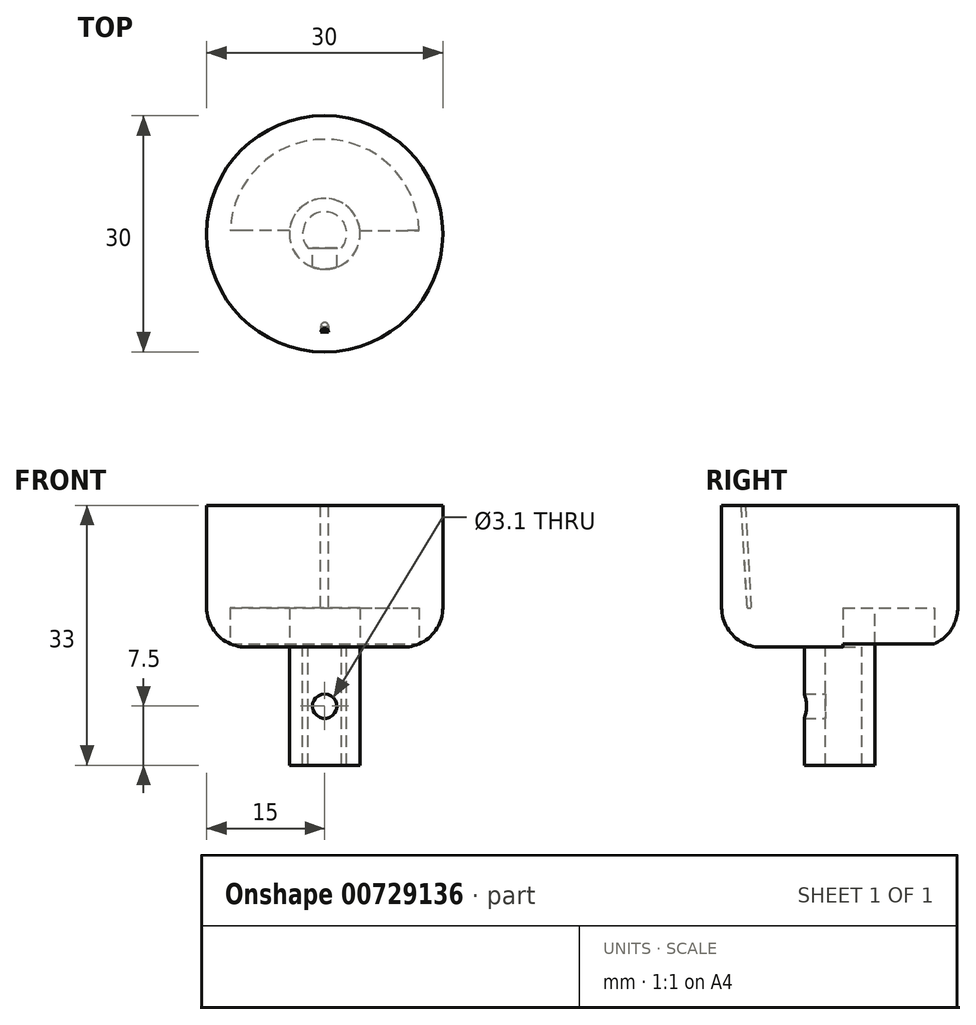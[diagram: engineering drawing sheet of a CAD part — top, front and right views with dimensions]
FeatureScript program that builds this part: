
annotation { "Feature Type Name" : "Feature", "Feature Type Description" : "" }
export const myFeature = defineFeature(function(context is Context, id is Id, definition is map)
    precondition{}
    {
        {
            var Q0;
            Q0=qCreatedBy(makeId("Top.planeOp"),FACE);
            var sketch = newSketch(context, id + "F0", { "sketchPlane" : qUnion([Q0])});
            skLineSegment(sketch, "E0", {"start": v(-2.14, -1.8) * mm, "end": v(2.14, -1.8) * mm});
            skArc(sketch, "E1", {"start": v(-2.14, -1.8) * mm, "mid": v(0, 2.8) * mm, "end": v(2.14, -1.8) * mm});
            skCircle(sketch, "E2", {"center": v(0, 0) * mm, "radius": 15 * mm});
            skCircle(sketch, "E3", {"center": v(0, 0) * mm, "radius": 4.5 * mm});
            skCircle(sketch, "E4", {"center": v(0, 0) * mm, "radius": 12 * mm});
            skSolve(sketch);
        }
        {
            var Q0;
            Q0=makeQuery(id+"F0.imprint","IMPRINT",FACE,{"disambiguationData":[TD([[makeQuery(id+"F0.imprint","IMPRINT",EDGE,{"derivedFrom":sQuery(id+"F0.wireOp",EDGE,"E0")}),-1.0]])]});
            var Q1;
            Q1=sQuery(id+"F0.wireOp",EDGE,"E1");
            var Q2;
            Q2=sQuery(id+"F0.wireOp",EDGE,"E0");
            extrude(context, id + "F1", {"entities" : qUnion([Q0]), "surfaceEntities" : qUnion([Q1, Q2]), "oppositeDirection" : true, "depth" : 15 * mm, "offsetDistance" : 25 * mm});
        }
        {
            var Q0;
            Q0=makeQuery(id+"F0.imprint","IMPRINT",FACE,{"disambiguationData":[TD([[makeQuery(id+"F0.imprint","IMPRINT",EDGE,{"derivedFrom":sQuery(id+"F0.wireOp",EDGE,"E3")}),-1.0]])]});
            var Q1;
            Q1=makeQuery(id+"F0.imprint","IMPRINT",FACE,{"disambiguationData":[TD([[makeQuery(id+"F0.imprint","IMPRINT",EDGE,{"derivedFrom":sQuery(id+"F0.wireOp",EDGE,"E0")}),1.0]])]});
            var Q2;
            Q2=makeQuery(id+"F0.imprint","IMPRINT",FACE,{"disambiguationData":[TD([[makeQuery(id+"F0.imprint","IMPRINT",EDGE,{"derivedFrom":sQuery(id+"F0.wireOp",EDGE,"E0")}),-1.0]])]});
            extrude(context, id + "F2", {"entities" : qUnion([Q0, Q1, Q2]), "operationType" : NewBodyOperationType.ADD, "depth" : 5 * mm, "offsetDistance" : 25 * mm});
        }
        {
            var Q0;
            {var subQ0=sQuery(id+"F0.wireOp",EDGE,"E0");Q0=makeQuery(id+"F2.boolean.opBoolean","MERGE",FACE,{"derivedFrom":[makeQuery(id+"F1.opExtrude","SWEPT_FACE",FACE,{"disambiguationData":[OSD([subQ0])]}),makeQuery(id+"F2.opExtrude","SWEPT_FACE",FACE,{"disambiguationData":[OSD([subQ0])]})]});}
            var sketch = newSketch(context, id + "F3", { "sketchPlane" : qUnion([Q0])});
            skPoint(sketch, "E5", {"position": v(0, -7.5) * mm});
            skSolve(sketch);
        }
        {
            var Q0;
            Q0=sQuery(id+"F3.wireOp",VERTEX,"E5");
            var Q1;
            Q1=makeQuery(id+"F1.opExtrude","SWEPT_BODY",BODY,{"disambiguationData":[OSD([sQuery(id+"F0.wireOp",EDGE,"E0"),sQuery(id+"F0.wireOp",EDGE,"E1"),sQuery(id+"F0.wireOp",EDGE,"E3")])]});
            hole(context, id + "F4", {"style" : HoleStyle.SIMPLE, "endStyle" : HoleEndStyle.THROUGH, "holeDiameter" : 3.1 * mm, "majorDiameter" : 5 * mm, "isTappedThrough" : true, "tappedDepth" : 12 * mm, "tapClearance" : 3, "locations" : qUnion([Q0]), "scope" : qUnion([Q1])});
        }
        {
            var Q0;
            Q0=qCreatedBy(makeId("Right.planeOp"),FACE);
            var sketch = newSketch(context, id + "F5", { "sketchPlane" : qUnion([Q0])});
            skLineSegment(sketch, "E6", {"start": v(11.75, 0) * mm, "end": v(15, 0) * mm});
            skLineSegment(sketch, "E7", {"start": v(15, 18) * mm, "end": v(12.5, 18) * mm});
            skLineSegment(sketch, "E8", {"start": v(15, 18) * mm, "end": v(15, 0) * mm});
            skLineSegment(sketch, "E9", {"start": v(11.75, 0) * mm, "end": v(11.75, 5) * mm});
            skLineSegment(sketch, "E10", {"start": v(11.75, 5) * mm, "end": v(12.5, 18) * mm});
            skLineSegment(sketch, "E11", {"start": v(0, 9.96) * mm, "end": v(0, -1.49) * mm, "construction": true});
            skSolve(sketch);
        }
        {
            var Q0;
            Q0=makeQuery(id+"F5.imprint","IMPRINT",FACE,{"disambiguationData":[TD([[makeQuery(id+"F5.imprint","IMPRINT",EDGE,{"derivedFrom":sQuery(id+"F5.wireOp",EDGE,"E6")}),1.0]])]});
            var Q1;
            Q1=sQuery(id+"F5.wireOp",EDGE,"E11");
            revolve(context, id + "F6", {"operationType" : NewBodyOperationType.ADD, "surfaceOperationType" : NewSurfaceOperationType.NEW, "entities" : qUnion([Q0]), "axis" : qUnion([Q1]), "revolveType" : RevolveType.FULL});
        }
        {
            var Q0;
            Q0=makeQuery(id+"F2.opExtrude","CAP_FACE",FACE,{"disambiguationData":[OSD([sQuery(id+"F0.wireOp",EDGE,"E4")])],"isStart":false});
            var sketch = newSketch(context, id + "F7", { "sketchPlane" : qUnion([Q0])});
            skCircle(sketch, "E12", {"center": v(0, 0) * mm, "radius": 11.75 * mm, "construction": true});
            skLineSegment(sketch, "E13", {"start": v(0.5, 11.74) * mm, "end": v(0.5, 11.74) * mm});
            skArc(sketch, "E14", {"start": v(-0.5, -11.74) * mm, "mid": v(0, -11.25) * mm, "end": v(0.5, -11.74) * mm});
            skSolve(sketch);
        }
        {
            var Q0;
            {var subQ0=sQuery(id+"F0.wireOp",EDGE,"E4");Q0=makeQuery(id+"F6.boolean.opBoolean","MERGE",FACE,{"derivedFrom":[makeQuery(id+"F2.boolean.opBoolean","SPLIT",FACE,{"disambiguationData":[TD([makeQuery(id+"F1.opExtrude","SWEPT_FACE",FACE,{"disambiguationData":[OSD([sQuery(id+"F0.wireOp",EDGE,"E3")])]})])],"derivedFrom":makeQuery(id+"F2.opExtrude","CAP_FACE",FACE,{"disambiguationData":[OSD([subQ0])],"isStart":true})}),makeQuery(id+"F6.opRevolve","SWEPT_FACE",FACE,{"disambiguationData":[OSD([sQuery(id+"F5.wireOp",EDGE,"E6")])]})]});}
            var sketch = newSketch(context, id + "F8", { "sketchPlane" : qUnion([Q0])});
            skCircle(sketch, "E15", {"center": v(0, 0) * mm, "radius": 12 * mm});
            skLineSegment(sketch, "E16", {"start": v(0, 0) * mm, "end": v(-12, 0) * mm, "construction": true});
            skCircle(sketch, "E17", {"center": v(0, 0) * mm, "radius": 4.5 * mm});
            skLineSegment(sketch, "E18", {"start": v(-4.48, -0.4) * mm, "end": v(-12, -0.4) * mm});
            skLineSegment(sketch, "E19", {"start": v(-4.48, 0.4) * mm, "end": v(-12, 0.4) * mm});
            skLineSegment(sketch, "E20", {"start": v(0, 0) * mm, "end": v(12, 0) * mm, "construction": true});
            skLineSegment(sketch, "E21", {"start": v(4.48, -0.4) * mm, "end": v(12, -0.4) * mm});
            skLineSegment(sketch, "E22", {"start": v(4.48, 0.4) * mm, "end": v(12, 0.4) * mm});
            skSolve(sketch);
        }
        {
            var Q0;
            Q0=makeQuery(id+"F6.opRevolve","SWEPT_FACE",FACE,{"disambiguationData":[OSD([sQuery(id+"F5.wireOp",EDGE,"E7")])]});
            var sketch = newSketch(context, id + "F9", { "sketchPlane" : qUnion([Q0])});
            skArc(sketch, "E23", {"start": v(-0.5, -12.49) * mm, "mid": v(0, -12) * mm, "end": v(0.5, -12.49) * mm});
            skSolve(sketch);
        }
        {
            var Q0;
            {var subQ0=sQuery(id+"F8.wireOp",EDGE,"E18");Q0=makeQuery(id+"F8.imprint","IMPRINT",FACE,{"disambiguationData":[TD([[makeQuery(id+"F8.imprint","IMPRINT",EDGE,{"derivedFrom":subQ0}),1.0]])]});}
            extrude(context, id + "F10", {"entities" : qUnion([Q0]), "operationType" : NewBodyOperationType.REMOVE, "oppositeDirection" : true, "depth" : 5 * mm, "offsetDistance" : 25 * mm});
        }
        {
            var Q1;
            {var subQ0=sQuery(id+"F7.wireOp",EDGE,"E14");Q1=makeQuery(id+"F7.imprint","IMPRINT",FACE,{"disambiguationData":[TD([[makeQuery(id+"F7.imprint","IMPRINT",EDGE,{"derivedFrom":subQ0}),-1.0]])]});}
            var Q2;
            {var subQ0=sQuery(id+"F9.wireOp",EDGE,"E23");Q2=makeQuery(id+"F9.imprint","IMPRINT",FACE,{"disambiguationData":[TD([[makeQuery(id+"F9.imprint","IMPRINT",EDGE,{"derivedFrom":subQ0}),-1.0]])]});}
            loft(context, id + "F11", {"operationType" : NewBodyOperationType.ADD, "sheetProfilesArray" : [{ "sheetProfileEntities" : qUnion([Q1]) }, { "sheetProfileEntities" : qUnion([Q2]) }]});
        }
        {
            var Q0;
            Q0=makeQuery(id+"F6.opRevolve","SWEPT_EDGE",EDGE,{"disambiguationData":[OSD([sQuery(id+"F5.wireOp",EDGE,"E6"),sQuery(id+"F5.wireOp",EDGE,"E8")])]});
            fillet(context, id + "F12", {"entities" : qUnion([Q0]), "radius" : 5 * mm, "tangentPropagation" : true, "allowEdgeOverflow" : false});
        }
    });
